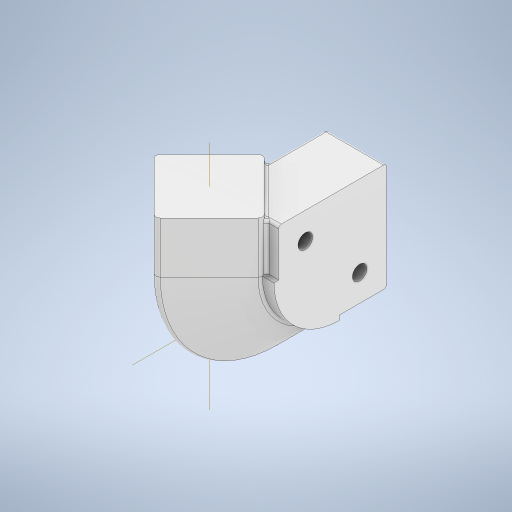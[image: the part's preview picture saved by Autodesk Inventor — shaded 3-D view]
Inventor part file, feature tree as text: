
AUTODESK INVENTOR PART (.ipt)
format: ipt  version: 2024 (Build 280153000, 153)  size: 440,832 bytes
history: native  units: mm
features: sketch x5, plane x3, fillet x3, other x2, hole x2, projected_geometry x2, sweep x1, extrude x1
ambient origin geometry x8: Origin, YZ Plane, XZ Plane, XY Plane, X Axis, Y Axis, Z Axis, Center Point
bodies: Solid1 (feature_tree)
feature tree (19):
  sketch  "Sketch2"  dims[d2=24.0mm d3=41.3mm d4=41.3mm d5=1.5mm d6=1.5mm]
  sketch  "Sketch1"  dims[d0=28.6mm d1=1.6mm]
  sweep  "Sweep1"
  plane  "Work Plane1"
  sketch  "Sketch3"  dims[d7=0.0mm d8=0.0mm d9=23.8mm]
  plane  "Work Plane2"
  extrude  "Extrusion1"  Depth=41.3mm
  fillet  "Fillet2"  Radius=41.3mm
  fillet  "Fillet3"  Radius=1.5mm
  fillet  "Fillet4"  Radius=1.5mm
  other  "Work Axis4"
  sketch  "Sketch6"  dims[d10=39.6mm d11=39.6mm]
  other  "Work Axis5"
  hole  "Hole2"  [1 undecoded]
  plane  "Work Plane4"
  hole  "Hole3"  [1 undecoded]
  projected_geometry  "Projected Loop1"
  sketch  "Sketch7"  dims[d14=0.2mm d15=0.2mm d16=1.5mm d17=48.0mm d18=22.5mm d19=1.7mm d20=10.0mm d21=0.0mm d32=20.0mm d33=20.0mm d36=1.0mm d37=1.0mm d38=1.0mm d39=0.2mm d40=0.2mm d41=5.4mm d42=6.0mm d43=4.0mm d44=2.0mm d45=90.0deg d46=8.0mm d47=20.594885mm d48=-15.0mm d49=9.5mm d50=6.0mm d51=4.0mm d52=2.0mm d53=90.0deg d54=8.0mm d55=20.594885mm]
  projected_geometry  "Project Cut Edges1"
note: 2 required parameter values undecoded (feature->parameter linkage not recoverable at this tier; creation-order binding heuristic only, values carry confidence <= 0.55)
